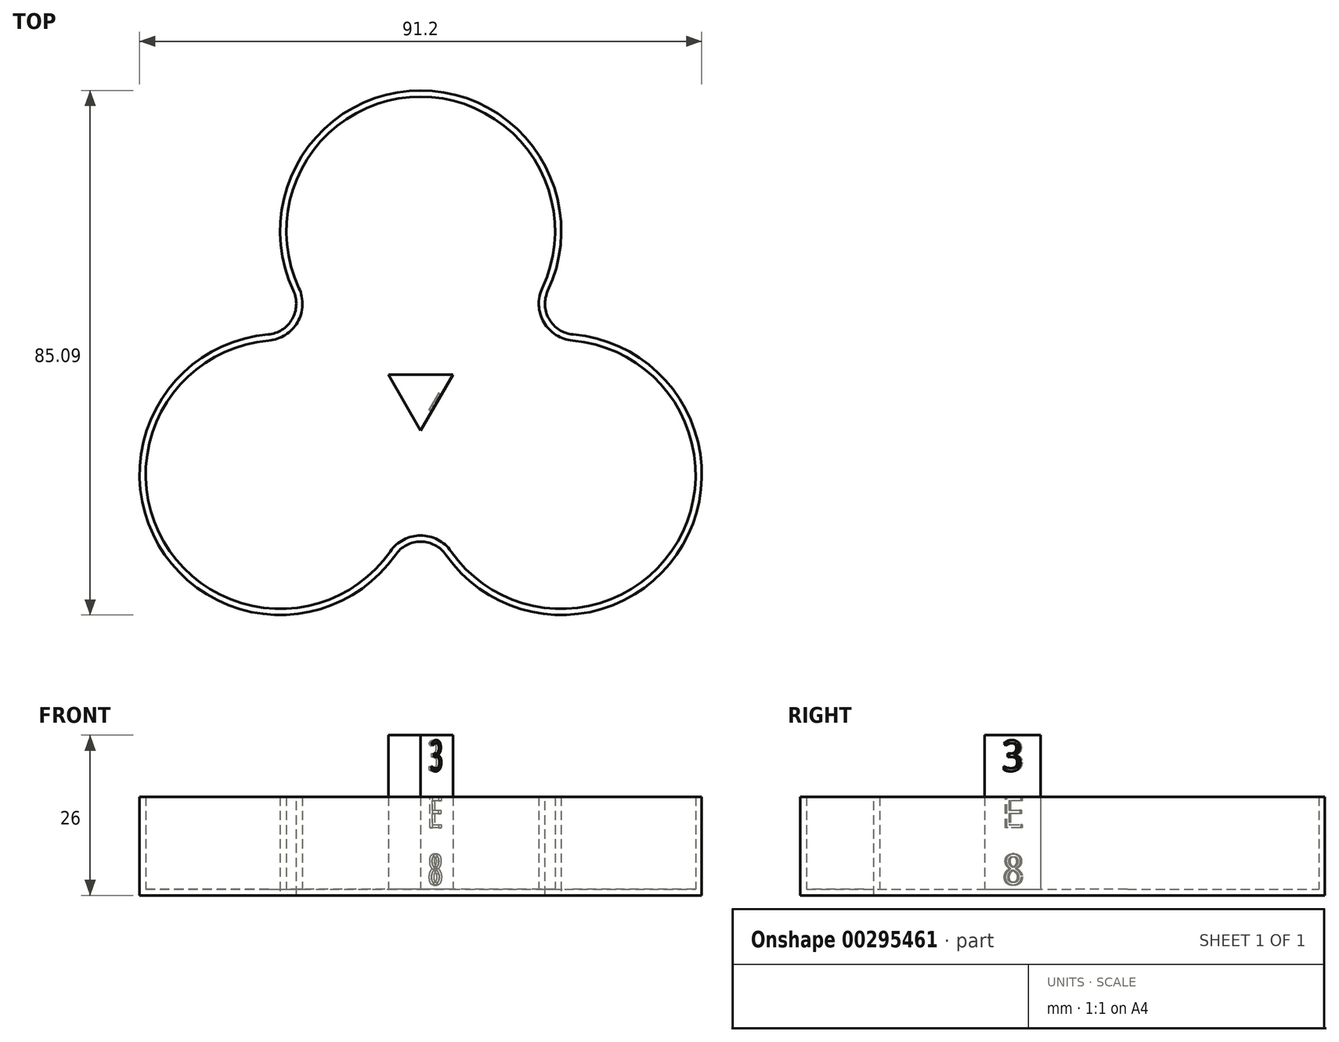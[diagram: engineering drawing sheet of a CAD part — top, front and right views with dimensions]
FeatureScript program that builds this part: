
annotation { "Feature Type Name" : "Feature", "Feature Type Description" : "" }
export const myFeature = defineFeature(function(context is Context, id is Id, definition is map)
    precondition{}
    {
        {
            var Q0;
            Q0=qCreatedBy(makeId("Top.planeOp"),FACE);
            var sketch = newSketch(context, id + "F0", { "sketchPlane" : qUnion([Q0])});
            skLineSegment(sketch, "E0", {"start": v(0, 0) * mm, "end": v(0, 26.33) * mm, "construction": true});
            skCircle(sketch, "E1", {"center": v(0, 26.33) * mm, "radius": 22.8 * mm});
            skCircle(sketch, "E2.1.0", {"center": v(22.8, -13.16) * mm, "radius": 22.8 * mm});
            skCircle(sketch, "E2.2.0", {"center": v(-22.8, -13.16) * mm, "radius": 22.8 * mm});
            skPoint(sketch, "E2.center", {"position": v(0, 0) * mm});
            skLineSegment(sketch, "E3", {"start": v(-22.8, -13.16) * mm, "end": v(0, 0) * mm, "construction": true});
            skLineSegment(sketch, "E4", {"start": v(0, 49.13) * mm, "end": v(0, 50.13) * mm, "construction": true});
            skSolve(sketch);
        }
        {
            var Q0;
            Q0 = qSketchRegion(id + "F0", true);
            var Q1;
            {var subQ0=sQuery(id+"F0.wireOp",EDGE,"E2.2.0");var subQ1=makeQuery(id+"F0.imprint","INTERSECT",VERTEX,{"derivedFrom":[sQuery(id+"F0.wireOp",EDGE,"E1"),subQ0]});Q1=makeQuery(id+"F0.imprint","IMPRINT",FACE,{"disambiguationData":[TD([[makeQuery(id+"F0.imprint","IMPRINT",EDGE,{"disambiguationData":[TD([[subQ1,1.0]])],"derivedFrom":subQ0}),1.0]])]});}
            var Q2;
            {var subQ0=sQuery(id+"F0.wireOp",EDGE,"E1");var subQ1=makeQuery(id+"F0.imprint","INTERSECT",VERTEX,{"derivedFrom":[subQ0,sQuery(id+"F0.wireOp",EDGE,"E2.1.0")]});Q2=makeQuery(id+"F0.imprint","IMPRINT",FACE,{"disambiguationData":[TD([[makeQuery(id+"F0.imprint","IMPRINT",EDGE,{"disambiguationData":[TD([[subQ1,1.0]])],"derivedFrom":subQ0}),1.0]])]});}
            var Q3;
            {var subQ0=sQuery(id+"F0.wireOp",EDGE,"E2.1.0");var subQ1=makeQuery(id+"F0.imprint","INTERSECT",VERTEX,{"derivedFrom":[sQuery(id+"F0.wireOp",EDGE,"E1"),subQ0]});Q3=makeQuery(id+"F0.imprint","IMPRINT",FACE,{"disambiguationData":[TD([[makeQuery(id+"F0.imprint","IMPRINT",EDGE,{"disambiguationData":[TD([[subQ1,-1.0]])],"derivedFrom":subQ0}),1.0]])]});}
            var Q4;
            {var subQ0=sQuery(id+"F0.wireOp",EDGE,"E2.1.0");var subQ1=sQuery(id+"F0.wireOp",EDGE,"E1");var subQ2=makeQuery(id+"F0.imprint","INTERSECT",VERTEX,{"derivedFrom":[subQ1,subQ0]});Q4=makeQuery(id+"F0.imprint","IMPRINT",FACE,{"disambiguationData":[TD([[makeQuery(id+"F0.imprint","IMPRINT",EDGE,{"disambiguationData":[TD([[subQ2,1.0]])],"derivedFrom":subQ1}),-1.0]])]});}
            extrude(context, id + "F1", {"entities" : qUnion([Q0, Q1, Q2, Q3, Q4]), "depth" : 1 * mm});
        }
        {
            var Q0;
            Q0=makeQuery(id+"F1.opExtrude","SWEPT_EDGE",EDGE,{"disambiguationData":[OSD([sQuery(id+"F0.wireOp",EDGE,"E1"),sQuery(id+"F0.wireOp",EDGE,"E2.2.0")])]});
            var Q1;
            Q1=makeQuery(id+"F1.opExtrude","SWEPT_EDGE",EDGE,{"disambiguationData":[OSD([sQuery(id+"F0.wireOp",EDGE,"E1"),sQuery(id+"F0.wireOp",EDGE,"E2.1.0")])]});
            var Q2;
            Q2=makeQuery(id+"F1.opExtrude","SWEPT_EDGE",EDGE,{"disambiguationData":[OSD([sQuery(id+"F0.wireOp",EDGE,"E2.1.0"),sQuery(id+"F0.wireOp",EDGE,"E2.2.0")])]});
            fillet(context, id + "F2", {"entities" : qUnion([Q0, Q1, Q2]), "radius" : 5 * mm, "tangentPropagation" : true, "allowEdgeOverflow" : false});
        }
        {
            var Q0;
            Q0=makeQuery(id+"F1.opExtrude","CAP_FACE",FACE,{"disambiguationData":[OSD([sQuery(id+"F0.wireOp",EDGE,"E1"),sQuery(id+"F0.wireOp",EDGE,"E2.1.0"),sQuery(id+"F0.wireOp",EDGE,"E2.2.0")])],"isStart":false});
            var sketch = newSketch(context, id + "F3", { "sketchPlane" : qUnion([Q0])});
            skArc(sketch, "E5.0", {"start": v(-4.1, -26.2) * mm, "mid": v(0, -24.07) * mm, "end": v(4.1, -26.2) * mm});
            skArc(sketch, "E6.0", {"start": v(-24.75, 9.55) * mm, "mid": v(-42.55, -24.56) * mm, "end": v(-4.1, -26.2) * mm});
            skArc(sketch, "E7.0", {"start": v(4.1, -26.2) * mm, "mid": v(42.55, -24.56) * mm, "end": v(24.75, 9.55) * mm});
            skArc(sketch, "E8.0", {"start": v(24.75, 9.55) * mm, "mid": v(20.84, 12.03) * mm, "end": v(20.65, 16.66) * mm});
            skArc(sketch, "E9.0", {"start": v(-20.65, 16.66) * mm, "mid": v(-20.84, 12.03) * mm, "end": v(-24.75, 9.55) * mm});
            skArc(sketch, "E10.0", {"start": v(20.65, 16.66) * mm, "mid": v(0, 49.13) * mm, "end": v(-20.65, 16.66) * mm});
            skCircle(sketch, "E11", {"center": v(22.8, -13.16) * mm, "radius": 21.8 * mm});
            skCircle(sketch, "E12", {"center": v(-22.8, -13.16) * mm, "radius": 21.8 * mm});
            skCircle(sketch, "E13", {"center": v(0, 26.33) * mm, "radius": 21.8 * mm});
            skArc(sketch, "E14.0", {"start": v(-4.92, -25.64) * mm, "mid": v(0, -23.07) * mm, "end": v(4.92, -25.64) * mm});
            skArc(sketch, "E15.1.0", {"start": v(24.66, 8.56) * mm, "mid": v(19.98, 11.53) * mm, "end": v(19.74, 17.08) * mm});
            skArc(sketch, "E15.2.0", {"start": v(-19.74, 17.08) * mm, "mid": v(-19.98, 11.53) * mm, "end": v(-24.66, 8.56) * mm});
            skPoint(sketch, "E15.center", {"position": v(0, 0) * mm});
            skLineSegment(sketch, "E16", {"start": v(7.84, 4.53) * mm, "end": v(-7.84, 4.53) * mm, "construction": true});
            skLineSegment(sketch, "E17", {"start": v(-7.84, 4.53) * mm, "end": v(0, -9.05) * mm, "construction": true});
            skLineSegment(sketch, "E18", {"start": v(0, -9.05) * mm, "end": v(7.84, 4.53) * mm, "construction": true});
            skLineSegment(sketch, "E19.0", {"start": v(0, -6.05) * mm, "end": v(5.24, 3.03) * mm});
            skLineSegment(sketch, "E19.1", {"start": v(-5.24, 3.03) * mm, "end": v(0, -6.05) * mm});
            skLineSegment(sketch, "E19.2", {"start": v(5.24, 3.03) * mm, "end": v(-5.24, 3.03) * mm});
            skSolve(sketch);
        }
        {
            var Q0;
            Q0 = qSketchRegion(id + "F3", true);
            var Q1;
            {var subQ0=sQuery(id+"F3.wireOp",EDGE,"E18");var subQ4=sQuery(id+"F3.wireOp",EDGE,"E16");var subQ7=makeQuery(id+"F3.imprint","INTERSECT",VERTEX,{"derivedFrom":[subQ4,subQ0]});Q1=makeQuery(id+"F3.imprint","IMPRINT",FACE,{"disambiguationData":[TD([[makeQuery(id+"F3.imprint","IMPRINT",EDGE,{"disambiguationData":[TD([[subQ7,-1.0]])],"derivedFrom":subQ4}),1.0]])]});}
            extrude(context, id + "F4", {"entities" : qUnion([Q0, Q1]), "operationType" : NewBodyOperationType.ADD, "depth" : 15 * mm});
        }
        {
            var Q0;
            Q0=makeQuery(id+"F3.imprint","IMPRINT",FACE,{"disambiguationData":[TD([[makeQuery(id+"F3.imprint","IMPRINT",EDGE,{"derivedFrom":sQuery(id+"F3.wireOp",EDGE,"E19.0")}),1.0]])]});
            extrude(context, id + "F5", {"entities" : qUnion([Q0]), "operationType" : NewBodyOperationType.ADD, "depth" : 25 * mm});
        }
        {
            var Q0;
            Q0=makeQuery(id+"F5.opExtrude","SWEPT_FACE",FACE,{"disambiguationData":[OSD([sQuery(id+"F3.wireOp",EDGE,"E19.0")])]});
            var sketch = newSketch(context, id + "F6", { "sketchPlane" : qUnion([Q0])});
            skText(sketch, "E20", { "text": "3\nE\n8", "fontName": "DroidSansMono.ttf"});
            const initialGuessF6  = {"E20": [-0.00211, 0.02018, 1, 0, 0.005]};
            skSetInitialGuess(sketch, initialGuessF6);
            skSolve(sketch);
        }
        {
            var Q0;
            Q0 = qSketchRegion(id + "F6", true);
            extrude(context, id + "F7", {"entities" : qUnion([Q0]), "operationType" : NewBodyOperationType.REMOVE, "oppositeDirection" : true, "depth" : .5 * mm});
        }
    });
